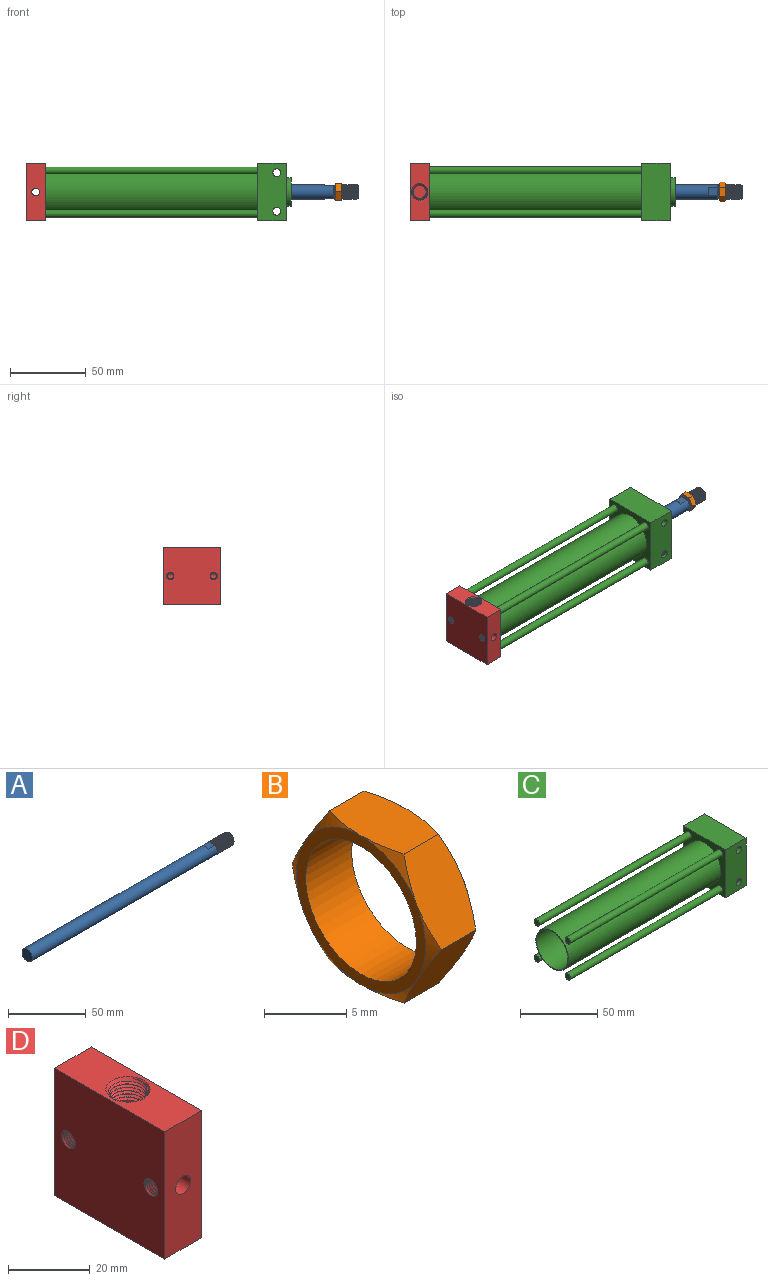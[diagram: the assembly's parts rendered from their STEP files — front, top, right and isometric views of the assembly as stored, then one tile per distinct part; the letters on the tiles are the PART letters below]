
ASSEMBLY  parts=4 mates=4
PART A: 17 faces, bbox 184.5x9.5x9.5 mm
  f0: plane 2.45x0.2mm, normal (-1,0,0), area 0.3mm2, adj f7,f8,f11
  f1: plane 2.44x0.18mm, normal (-1,0,0), area 0.3mm2, adj f8,f12
  f2: cylinder r=4.76mm len=14.56mm, axis (-1,0,0), area 54.5mm2, adj f3,f4,f5,f8
  f3: bspline ~16.23x9.53mm, area 318.9mm2, adj f2,f5,f7,f8
  f4: bspline ~16.23x9.53mm, area 318.7mm2, adj f2,f5,f7,f8
  f5: cone r=4.06mm half-angle=45deg, axis (-1,0,0), area 15.3mm2, adj f2,f3,f4,f6,f7
  f6: plane 8.11x8.11mm, normal (1,0,0), area 51.7mm2, adj f5
  f7: bspline ~16.02x8.29mm, area 51.5mm2, adj f0,f3,f4,f5,f9
  f8: cone r=4.15mm half-angle=45deg, axis (1,0,0), area 11.9mm2, adj f0,f1,f2,f3,f4,f9,f13
  f9: plane 7.96x3.57mm, normal (1,0,0), area 6mm2, adj f7,f8,f10,f11,f12
  f10: cylinder r=4.76mm len=168.28mm, axis (1,0,0), area 4964.6mm2, adj f9,f11,f12,f13,f14,f15,f16
  f11: plane 6.35x5.27mm, normal (0,0,-1), area 33.4mm2, adj f0,f9,f10,f13,f14
  f12: plane 6.35x5.27mm, normal (0,0,1), area 33.4mm2, adj f1,f9,f10,f13,f15
  f13: plane 7.94x3.54mm, normal (1,0,0), area 6mm2, adj f8,f10,f11,f12
  f14: plane 5.27x0.79mm, normal (1,0,0), area 2.8mm2, adj f10,f11
  f15: plane 5.27x0.79mm, normal (1,0,0), area 2.8mm2, adj f10,f12
  f16: plane 9.53x9.53mm, normal (-1,0,0), area 71.3mm2, adj f10
PART B: 21 faces, bbox 4.5x13.4x13.4 mm
  f0: plane 6.08x4.5mm, normal (0,-0.87,0.5), area 23.2mm2, adj f1,f5,f10,f11,f16,f17
  f1: plane 6.95x4.5mm, normal (0,0,1), area 23.2mm2, adj f0,f2,f11,f12,f17,f18
  f2: plane 6.08x4.5mm, normal (0,0.87,0.5), area 23.2mm2, adj f1,f3,f12,f13,f18,f19
  f3: plane 6.08x4.5mm, normal (0,0.87,-0.5), area 23.2mm2, adj f2,f4,f13,f14,f19,f20
  f4: plane 6.95x4.5mm, normal (0,0,-1), area 23.2mm2, adj f3,f5,f9,f14,f15,f20
  f5: plane 6.08x4.5mm, normal (0,-0.87,-0.5), area 23.2mm2, adj f0,f4,f9,f10,f15,f16
  f6: plane 11.11x11.11mm, normal (-1,0,0), area 25.7mm2, adj f8,f15,f16,f17,f18,f19,f20
  f7: plane 11.11x11.11mm, normal (1,0,0), area 25.7mm2, adj f8,f9,f10,f11,f12,f13,f14
  f8: cylinder r=4.76mm len=9.53mm, axis (1,0,0), area 118.6mm2, adj f6,f7
  f9: cone r=5.56mm half-angle=60deg, axis (-1,0,0), area 3mm2, adj f4,f5,f7
  f10: cone r=5.56mm half-angle=60deg, axis (-1,0,0), area 3mm2, adj f0,f5,f7
  f11: cone r=5.56mm half-angle=60deg, axis (-1,0,0), area 3mm2, adj f0,f1,f7
  f12: cone r=5.56mm half-angle=60deg, axis (-1,0,0), area 3mm2, adj f1,f2,f7
  f13: cone r=5.56mm half-angle=60deg, axis (-1,0,0), area 3mm2, adj f2,f3,f7
  f14: cone r=5.56mm half-angle=60deg, axis (-1,0,0), area 3mm2, adj f3,f4,f7
  f15: cone r=5.56mm half-angle=60deg, axis (1,0,0), area 3mm2, adj f4,f5,f6
  f16: cone r=5.56mm half-angle=60deg, axis (1,0,0), area 3mm2, adj f0,f5,f6
  f17: cone r=5.56mm half-angle=60deg, axis (1,0,0), area 3mm2, adj f0,f1,f6
  f18: cone r=5.56mm half-angle=60deg, axis (1,0,0), area 3mm2, adj f1,f2,f6
  f19: cone r=5.56mm half-angle=60deg, axis (1,0,0), area 3mm2, adj f2,f3,f6
  f20: cone r=5.56mm half-angle=60deg, axis (1,0,0), area 3mm2, adj f3,f4,f6
PART C: 102 faces, bbox 162.3x38.8x38.5 mm
  f0: plane 38.1x38.1mm, normal (-1,0,0), area 671.4mm2, adj f1,f3,f5,f87,f88,f89,f97,f98
  f1: cylinder r=2.41mm len=139.7mm, axis (1,0,0), area 2118mm2, adj f0,f2
  f2: plane 4.83x4.83mm, normal (-1,0,0), area 18.3mm2, adj f1
  f3: cylinder r=2.41mm len=139.7mm, axis (1,0,0), area 2118mm2, adj f0,f4
  f4: plane 4.83x4.83mm, normal (-1,0,0), area 18.3mm2, adj f3
  f5: cylinder r=15mm len=139.7mm, axis (1,0,0), area 13168.1mm2, adj f0,f6
  f6: plane 30x30mm, normal (-1,0,0), area 65.7mm2, adj f5,f7
  f7: cylinder r=14.29mm len=139.7mm, axis (1,0,0), area 12541mm2, adj f6,f8
  f8: plane 28.58x28.58mm, normal (-1,0,0), area 570mm2, adj f7,f9
  f9: cylinder r=4.76mm len=22.23mm, axis (1,0,0), area 665.1mm2, adj f8,f10
  f10: plane 19.05x19.05mm, normal (1,0,0), area 213.8mm2, adj f9,f11
  f11: cylinder r=9.53mm len=19.05mm, axis (1,0,0), area 190mm2, adj f10,f12
  f12: plane 38.1x38.1mm, normal (1,0,0), area 1093.4mm2, adj f11,f13,f45,f46,f82,f83,f84,f85
  f13: cone r=2.41mm half-angle=45deg, axis (1,0,0), area 5.1mm2, adj f12,f14,f43,f44
  f14: bspline ~3.79x3.79mm, area 4.9mm2, adj f13,f15,f43,f44
  f15: cylinder r=2.59mm len=38.1mm, axis (0,1,0), area 587.1mm2, adj f14,f16,f17,f18,f19,f20,f21,f22
  f16: plane 4.39x1.41mm, normal (1,0,0), area 4.4mm2, adj f15,f30
  f17: bspline ~3.79x3.79mm, area 4.9mm2, adj f15,f18,f19,f85
  f18: bspline ~4.83x4.83mm, area 37mm2, adj f15,f17,f85,f86
  f19: bspline ~4.82x4.81mm, area 40.4mm2, adj f15,f17,f20,f85,f86
  f20: bspline ~3.8x3.24mm, area 0.6mm2, adj f15,f19,f21
  f21: bspline ~4.82x2.94mm, area 4mm2, adj f15,f20,f22
  f22: cylinder r=2.41mm len=4.78mm, axis (1,0,0), area 0.7mm2, adj f15,f21,f23
  f23: bspline ~4.83x2.41mm, area 3.4mm2, adj f15,f22,f24
  f24: bspline ~3.8x1.9mm, area 0.5mm2, adj f15,f23,f25
  f25: bspline ~4.83x2.41mm, area 3.2mm2, adj f15,f24,f26
  f26: cylinder r=2.41mm len=4.55mm, axis (1,0,0), area 0.6mm2, adj f15,f25,f27
  f27: bspline ~4.83x2.41mm, area 2.9mm2, adj f15,f26,f28
  f28: bspline ~3.31x1mm, area 0.4mm2, adj f15,f27,f29
  f29: bspline ~4.4x1.64mm, area 2.8mm2, adj f15,f28,f30
  f30: cylinder r=2.41mm len=4.4mm, axis (1,0,0), area 1.1mm2, adj f15,f16,f29
  f31: bspline ~3.8x3.24mm, area 0.6mm2, adj f15,f32,f43
  f32: bspline ~4.82x2.94mm, area 4mm2, adj f15,f31,f33
  f33: cylinder r=2.41mm len=4.78mm, axis (1,0,0), area 0.7mm2, adj f15,f32,f34
  f34: bspline ~4.83x2.41mm, area 3.4mm2, adj f15,f33,f35
  f35: bspline ~3.8x1.9mm, area 0.5mm2, adj f15,f34,f36
  f36: bspline ~4.83x2.41mm, area 3.2mm2, adj f15,f35,f37
  f37: cylinder r=2.41mm len=4.55mm, axis (1,0,0), area 0.6mm2, adj f15,f36,f38
  f38: bspline ~4.83x2.41mm, area 2.9mm2, adj f15,f37,f39
  f39: bspline ~3.31x1mm, area 0.4mm2, adj f15,f38,f40
  f40: bspline ~4.4x1.64mm, area 2.8mm2, adj f15,f39,f41
  f41: cylinder r=2.41mm len=4.4mm, axis (1,0,0), area 1.1mm2, adj f15,f40,f42
  f42: plane 4.39x1.41mm, normal (1,0,0), area 4.4mm2, adj f15,f41
  f43: bspline ~4.82x4.81mm, area 40.4mm2, adj f13,f14,f15,f31,f45
  f44: bspline ~4.83x4.83mm, area 37mm2, adj f13,f14,f15,f45
  f45: cylinder r=2.41mm len=4.83mm, axis (1,0,0), area 9.5mm2, adj f12,f15,f43,f44
  f46: cone r=2.41mm half-angle=45deg, axis (1,0,0), area 5.1mm2, adj f12,f47,f80,f81
  f47: bspline ~3.8x3.8mm, area 5.3mm2, adj f46,f48,f80,f81
  f48: cylinder r=2.59mm len=38.1mm, axis (0,1,0), area 583.5mm2, adj f47,f49,f50,f51,f52,f53,f54,f55
  f49: bspline ~3.41x1.07mm, area 0mm2, adj f48,f84
  f50: bspline ~4.83x4.83mm, area 36.9mm2, adj f48,f51,f83,f84
  f51: bspline ~3.8x3.8mm, area 5.3mm2, adj f48,f50,f52,f83
  f52: bspline ~4.83x4.83mm, area 40.5mm2, adj f48,f51,f53,f83,f84
  f53: cylinder r=2.41mm len=4.83mm, axis (1,0,0), area 0.8mm2, adj f48,f52,f54
  f54: bspline ~4.82x2.81mm, area 3.9mm2, adj f48,f53,f55
  f55: bspline ~3.8x1.9mm, area 0.5mm2, adj f48,f54,f56
  f56: bspline ~4.83x2.41mm, area 3.5mm2, adj f48,f55,f57
  f57: cylinder r=2.41mm len=4.68mm, axis (1,0,0), area 0.6mm2, adj f48,f56,f58
  f58: bspline ~4.83x2.41mm, area 3.1mm2, adj f48,f57,f59
  f59: bspline ~3.8x1.9mm, area 0.4mm2, adj f48,f58,f60
  f60: bspline ~4.83x2.41mm, area 2.9mm2, adj f48,f59,f61
  f61: cylinder r=2.41mm len=4.45mm, axis (1,0,0), area 0.6mm2, adj f48,f60,f65
  f62: plane 3.9x1.28mm, normal (1,0,0), area 2.8mm2, adj f48,f63,f64
  f63: bspline ~4.12x2.41mm, area 0.9mm2, adj f48,f62,f64
  f64: bspline ~3.23x0.91mm, area 0.4mm2, adj f48,f62,f63,f65
  f65: bspline ~4.44x1.69mm, area 2.8mm2, adj f48,f61,f64
  f66: bspline ~3.41x1.07mm, area 0mm2, adj f48,f82
  f67: cylinder r=2.41mm len=4.83mm, axis (1,0,0), area 0.8mm2, adj f48,f68,f81
  f68: bspline ~4.82x2.81mm, area 3.9mm2, adj f48,f67,f69
  f69: bspline ~3.8x1.9mm, area 0.5mm2, adj f48,f68,f70
  f70: bspline ~4.83x2.41mm, area 3.5mm2, adj f48,f69,f71
  f71: cylinder r=2.41mm len=4.68mm, axis (1,0,0), area 0.6mm2, adj f48,f70,f72
  f72: bspline ~4.83x2.41mm, area 3.1mm2, adj f48,f71,f73
  f73: bspline ~3.8x1.9mm, area 0.4mm2, adj f48,f72,f74
  f74: bspline ~4.83x2.41mm, area 2.9mm2, adj f48,f73,f75
  f75: cylinder r=2.41mm len=4.45mm, axis (1,0,0), area 0.6mm2, adj f48,f74,f79
  f76: plane 3.9x1.28mm, normal (1,0,0), area 2.8mm2, adj f48,f77,f78
  f77: bspline ~4.12x2.41mm, area 0.9mm2, adj f48,f76,f78
  f78: bspline ~3.23x0.91mm, area 0.4mm2, adj f48,f76,f77,f79
  f79: bspline ~4.44x1.69mm, area 2.8mm2, adj f48,f75,f78
  f80: bspline ~4.83x4.83mm, area 36.9mm2, adj f46,f47,f48,f82
  f81: bspline ~4.83x4.83mm, area 40.5mm2, adj f46,f47,f48,f67,f82
  f82: cylinder r=2.41mm len=4.83mm, axis (1,0,0), area 6.8mm2, adj f12,f48,f66,f80,f81
  f83: cone r=2.41mm half-angle=45deg, axis (1,0,0), area 5.1mm2, adj f12,f50,f51,f52
  f84: cylinder r=2.41mm len=4.83mm, axis (1,0,0), area 6.8mm2, adj f12,f48,f49,f50,f52
  f85: cone r=2.41mm half-angle=45deg, axis (1,0,0), area 5.1mm2, adj f12,f17,f18,f19
  f86: cylinder r=2.41mm len=4.83mm, axis (1,0,0), area 9.5mm2, adj f12,f15,f18,f19
  f87: plane 38.1x19.05mm, normal (0,-1,0), area 683.6mm2, adj f0,f12,f15,f48,f88,f97
  f88: plane 38.1x19.05mm, normal (0,0,-1), area 725.8mm2, adj f0,f12,f87,f89
  f89: plane 38.1x19.05mm, normal (0,1,0), area 592.1mm2, adj f0,f12,f15,f48,f88,f90,f97
  f90: cone r=5.4mm half-angle=45deg, axis (0,1,0), area 24.5mm2, adj f89,f91,f94,f95,f96
  f91: bspline ~10.48x10.47mm, area 50.7mm2, adj f90,f92,f93,f94,f96
  f92: plane 9.58x9.58mm, normal (0,1,0), area 66.3mm2, adj f91,f93,f95,f96
  f93: bspline ~9.07x9.06mm, area 23.1mm2, adj f91,f92,f94,f95
  f94: cone r=5.4mm half-angle=45deg, axis (0,1,0), area 2mm2, adj f90,f91,f93,f95
  f95: bspline ~10.51x10.5mm, area 162.9mm2, adj f90,f92,f93,f94,f96
  f96: cone r=5.14mm half-angle=1.8deg, axis (0,1,0), area 26.6mm2, adj f90,f91,f92,f95
  f97: plane 38.1x19.05mm, normal (0,0,1), area 725.8mm2, adj f0,f12,f87,f89
  f98: cylinder r=2.41mm len=139.7mm, axis (1,0,0), area 2118mm2, adj f0,f99
  f99: plane 4.83x4.83mm, normal (-1,0,0), area 18.3mm2, adj f98
  f100: cylinder r=2.41mm len=139.7mm, axis (1,0,0), area 2118mm2, adj f0,f101
  f101: plane 4.83x4.83mm, normal (-1,0,0), area 18.3mm2, adj f100
PART D: 33 faces, bbox 13x38.1x38.3 mm
  f0: cylinder r=2.41mm len=3.96mm, axis (-1,0,0), area 0mm2, adj f1,f32
  f1: cylinder r=2.59mm len=38.1mm, axis (0,1,0), area 581.4mm2, adj f0,f2,f3,f18,f19,f20,f21,f22
  f2: cylinder r=2.41mm len=3.05mm, axis (-1,0,0), area 0mm2, adj f1,f21
  f3: bspline ~3.8x3.8mm, area 5.1mm2, adj f1,f4,f19,f32
  f4: cone r=2.41mm half-angle=45deg, axis (-1,0,0), area 5.1mm2, adj f3,f5,f19,f32
  f5: plane 38.1x38.1mm, normal (-1,0,0), area 1415mm2, adj f4,f6,f8,f17,f18,f26,f30,f31
  f6: plane 38.1x12.7mm, normal (0,0,-1), area 483.9mm2, adj f5,f7,f30,f31
  f7: plane 38.1x38.1mm, normal (1,0,0), area 1451.6mm2, adj f6,f8,f30,f31
  f8: plane 38.1x12.7mm, normal (0,0,1), area 392.3mm2, adj f5,f7,f9,f30,f31
  f9: cone r=5.4mm half-angle=45deg, axis (0,0,1), area 25mm2, adj f8,f10,f14,f15,f16
  f10: cone r=5.14mm half-angle=1.8deg, axis (0,0,1), area 36.6mm2, adj f9,f11,f13,f14,f16
  f11: plane 0.84x0.52mm, normal (0.81,-0.59,0), area 0.3mm2, adj f10,f12,f14,f16
  f12: bspline ~9.05x8.99mm, area 21.7mm2, adj f11,f14,f15,f16
  f13: plane 9.81x9.81mm, normal (0,0,1), area 75.6mm2, adj f10,f14
  f14: bspline ~10.46x10.43mm, area 152.5mm2, adj f9,f10,f11,f12,f13,f15
  f15: cone r=5.4mm half-angle=45deg, axis (0,0,1), area 1.5mm2, adj f9,f12,f14,f16
  f16: bspline ~10.49x10.49mm, area 147.9mm2, adj f9,f10,f11,f12,f15
  f17: cone r=2.41mm half-angle=45deg, axis (-1,0,0), area 5.1mm2, adj f5,f23,f25,f27
  f18: cylinder r=2.41mm len=4.83mm, axis (-1,0,0), area 7mm2, adj f1,f5,f19,f32
  f19: bspline ~4.83x4.83mm, area 39.4mm2, adj f1,f3,f4,f18,f20
  f20: bspline ~3.24x1.9mm, area 0.3mm2, adj f1,f19,f21
  f21: bspline ~3.41x1.07mm, area 1.7mm2, adj f1,f2,f20
  f22: cylinder r=2.41mm len=3.05mm, axis (-1,0,0), area 0mm2, adj f1,f29
  f23: bspline ~3.8x3.8mm, area 5.1mm2, adj f1,f17,f25,f27
  f24: cylinder r=2.41mm len=3.96mm, axis (-1,0,0), area 0mm2, adj f1,f25
  f25: bspline ~4.83x4.83mm, area 39mm2, adj f1,f17,f23,f24,f26
  f26: cylinder r=2.41mm len=4.83mm, axis (-1,0,0), area 7mm2, adj f1,f5,f25,f27
  f27: bspline ~4.83x4.83mm, area 39.4mm2, adj f1,f17,f23,f26,f28
  f28: bspline ~3.24x1.9mm, area 0.3mm2, adj f1,f27,f29
  f29: bspline ~3.41x1.07mm, area 1.7mm2, adj f1,f22,f28
  f30: plane 38.1x12.7mm, normal (0,1,0), area 462.8mm2, adj f1,f5,f6,f7,f8
  f31: plane 38.1x12.7mm, normal (0,-1,0), area 462.8mm2, adj f1,f5,f6,f7,f8
  f32: bspline ~4.8x4.79mm, area 39mm2, adj f0,f1,f3,f4,f18
PLACE A t=(-237.22,-81.34,-21.81)mm
PLACE B t=(-238.61,-81.34,-21.81)mm
PLACE C t=(-144.62,-81.34,-21.81)mm
PLACE D t=(-144.62,-81.34,-21.81)mm
MATE fastened D.f7 <-> C.f5  axis (1,0,0) through (-131.92,-81.34,-21.81)mm
MATE slider A.f2 <-> C.f5  axis (1,0,0) through (-26.08,-81.34,-21.81)mm
MATE slider B.f8 <-> A.f2  axis (1,0,0) through (61.03,-81.34,-21.81)mm
MATE fastened A.f2 <-> B.f8  axis (1,0,0) through (73.93,-81.34,-21.81)mm
